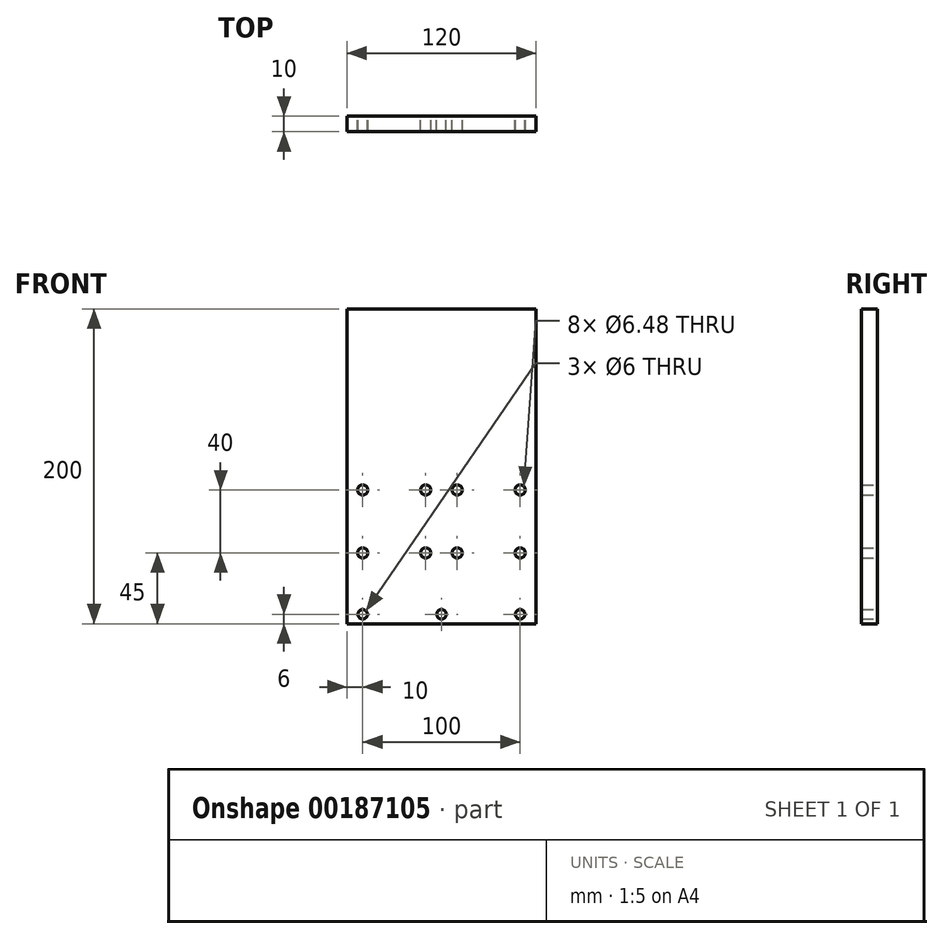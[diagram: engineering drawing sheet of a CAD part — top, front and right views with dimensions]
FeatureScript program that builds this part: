
annotation { "Feature Type Name" : "Feature", "Feature Type Description" : "" }
export const myFeature = defineFeature(function(context is Context, id is Id, definition is map)
    precondition{}
    {
        {
            var Q0;
            Q0=qCreatedBy(makeId("Front.planeOp"),FACE);
            var sketch = newSketch(context, id + "F0", { "sketchPlane" : qUnion([Q0])});
            skLineSegment(sketch, "E0.bottom", {"start": v(60, -100) * mm, "end": v(-60, -100) * mm});
            skLineSegment(sketch, "E0.top", {"start": v(60, 100) * mm, "end": v(-60, 100) * mm});
            skLineSegment(sketch, "E0.left", {"start": v(60, -100) * mm, "end": v(60, 100) * mm});
            skLineSegment(sketch, "E0.right", {"start": v(-60, -100) * mm, "end": v(-60, 100) * mm});
            skPoint(sketch, "E0.middle", {"position": v(0, 0) * mm});
            skCircle(sketch, "E1", {"center": v(-50, -15) * mm, "radius": 3.24 * mm});
            skCircle(sketch, "E2", {"center": v(-10, -15) * mm, "radius": 3.24 * mm});
            skCircle(sketch, "E3", {"center": v(-10, -55) * mm, "radius": 3.24 * mm});
            skCircle(sketch, "E4", {"center": v(-50, -55) * mm, "radius": 3.24 * mm});
            skCircle(sketch, "E5", {"center": v(10, -55) * mm, "radius": 3.24 * mm});
            skCircle(sketch, "E6", {"center": v(10, -15) * mm, "radius": 3.24 * mm});
            skCircle(sketch, "E7", {"center": v(50, -15) * mm, "radius": 3.24 * mm});
            skCircle(sketch, "E8", {"center": v(50, -55) * mm, "radius": 3.24 * mm});
            skCircle(sketch, "E9", {"center": v(-50, -94) * mm, "radius": 3 * mm});
            skCircle(sketch, "E10", {"center": v(0, -94) * mm, "radius": 3 * mm});
            skCircle(sketch, "E11", {"center": v(50, -94) * mm, "radius": 3 * mm});
            skSolve(sketch);
        }
        {
            var Q0;
            Q0=makeQuery(id+"F0.imprint","IMPRINT",FACE,{"disambiguationData":[TD([[makeQuery(id+"F0.imprint","IMPRINT",EDGE,{"derivedFrom":sQuery(id+"F0.wireOp",EDGE,"E0.bottom")}),-1.0]])]});
            extrude(context, id + "F1", {"entities" : qUnion([Q0]), "depth" : 10 * mm});
        }
    });
